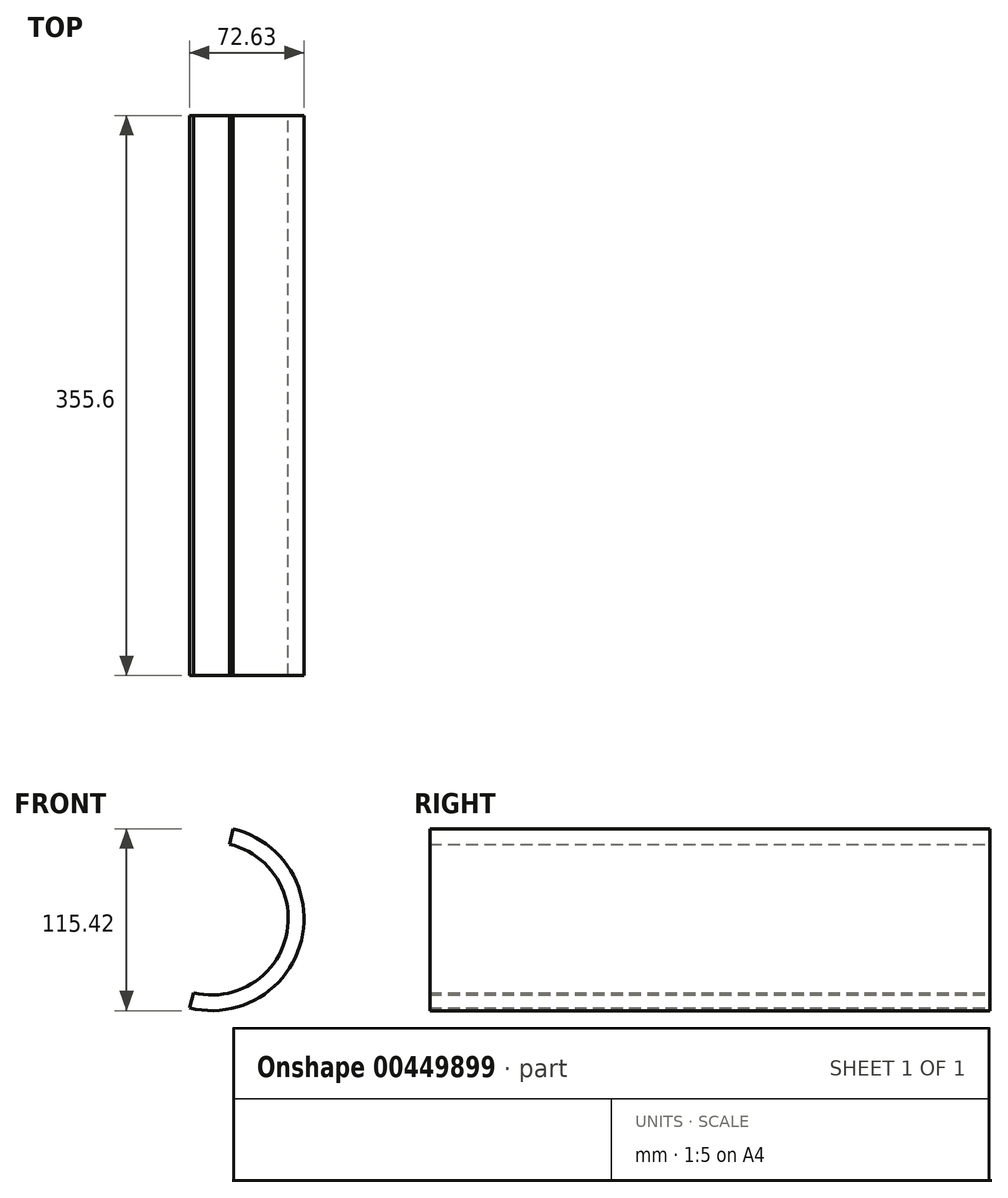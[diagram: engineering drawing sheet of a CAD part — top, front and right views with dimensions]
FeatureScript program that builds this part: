
annotation { "Feature Type Name" : "Feature", "Feature Type Description" : "" }
export const myFeature = defineFeature(function(context is Context, id is Id, definition is map)
    precondition{}
    {
        {
            var Q0;
            Q0=qCreatedBy(makeId("Front.planeOp"),FACE);
            var sketch = newSketch(context, id + "F0", { "sketchPlane" : qUnion([Q0])});
            skArc(sketch, "E0", {"start": v(-14.12, -56.78) * mm, "mid": v(56.85, -13.87) * mm, "end": v(13.61, 56.9) * mm});
            skArc(sketch, "E1", {"start": v(-11.75, -47.07) * mm, "mid": v(47.13, -11.5) * mm, "end": v(11.24, 47.2) * mm});
            skLineSegment(sketch, "E2", {"start": v(13.61, 56.9) * mm, "end": v(11.24, 47.2) * mm});
            skLineSegment(sketch, "E3", {"start": v(-14.12, -56.78) * mm, "end": v(-11.75, -47.07) * mm});
            skLineSegment(sketch, "E4.trimOffspring", {"start": v(-11.75, -47.07) * mm, "end": v(-14.12, -56.78) * mm});
            skSolve(sketch);
        }
        {
            var Q0;
            Q0=makeQuery(id+"F0.imprint","IMPRINT",FACE,{"disambiguationData":[TD([[makeQuery(id+"F0.imprint","IMPRINT",EDGE,{"derivedFrom":sQuery(id+"F0.wireOp",EDGE,"E0")}),1.0]])]});
            extrude(context, id + "F1", {"entities" : qUnion([Q0]), "depth" : 355.6 * mm});
        }
    });
